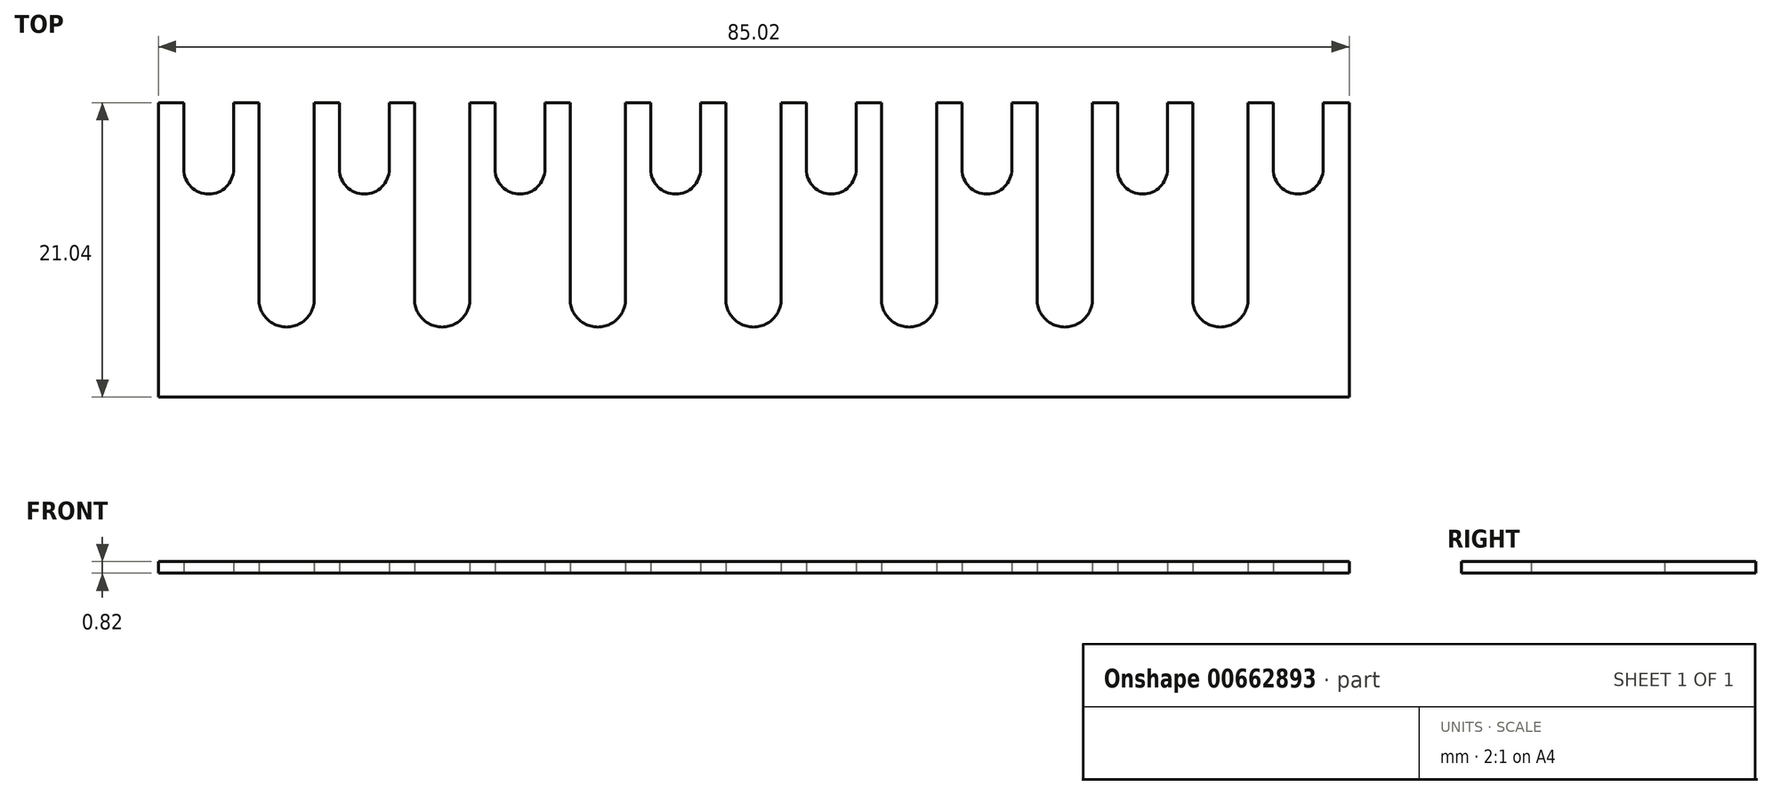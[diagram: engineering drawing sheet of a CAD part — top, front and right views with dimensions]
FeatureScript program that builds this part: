
annotation { "Feature Type Name" : "Feature", "Feature Type Description" : "" }
export const myFeature = defineFeature(function(context is Context, id is Id, definition is map)
    precondition{}
    {
        {
            var Q0;
            Q0=qCreatedBy(makeId("Top.planeOp"),FACE);
            var sketch = newSketch(context, id + "F0", { "sketchPlane" : qUnion([Q0])});
            skLineSegment(sketch, "E0.top", {"start": v(42.5, -10.52) * mm, "end": v(0, -10.52) * mm});
            skLineSegment(sketch, "E0.right", {"start": v(-42.5, 10.52) * mm, "end": v(-42.5, -10.52) * mm});
            skPoint(sketch, "E0.middle", {"position": v(0, 0) * mm});
            skPoint(sketch, "E1.endSnap0", {"position": v(0, 10.52) * mm});
            skLineSegment(sketch, "E2", {"start": v(-40.7, 5.77) * mm, "end": v(-40.7, 10.52) * mm});
            skLineSegment(sketch, "E3", {"start": v(-37.15, 10.52) * mm, "end": v(-37.15, 5.77) * mm});
            skLineSegment(sketch, "E4.trimOffspring", {"start": v(-40.7, 10.52) * mm, "end": v(-42.5, 10.52) * mm});
            skArc(sketch, "E5", {"start": v(-40.7, 5.77) * mm, "mid": v(-38.93, 3.99) * mm, "end": v(-37.15, 5.77) * mm});
            skLineSegment(sketch, "E6", {"start": v(-37.15, 10.52) * mm, "end": v(-35.34, 10.52) * mm});
            skLineSegment(sketch, "E7", {"start": v(-35.34, 10.52) * mm, "end": v(-35.34, -3.54) * mm});
            skLineSegment(sketch, "E8", {"start": v(0, -10.52) * mm, "end": v(-42.5, -10.52) * mm});
            skArc(sketch, "E9", {"start": v(-35.34, -3.54) * mm, "mid": v(-33.37, -5.51) * mm, "end": v(-31.4, -3.54) * mm});
            skLineSegment(sketch, "E10", {"start": v(-31.4, 10.52) * mm, "end": v(-31.4, -3.54) * mm});
            skLineSegment(sketch, "E11", {"start": v(-29.6, 5.77) * mm, "end": v(-29.6, 10.52) * mm});
            skLineSegment(sketch, "E12", {"start": v(-26.03, 10.52) * mm, "end": v(-26.03, 5.77) * mm});
            skLineSegment(sketch, "E13.trimOffspring", {"start": v(-29.6, 10.52) * mm, "end": v(-31.4, 10.52) * mm});
            skArc(sketch, "E14", {"start": v(-29.6, 5.77) * mm, "mid": v(-27.81, 3.99) * mm, "end": v(-26.03, 5.77) * mm});
            skLineSegment(sketch, "E15", {"start": v(-26.03, 10.52) * mm, "end": v(-24.23, 10.52) * mm});
            skLineSegment(sketch, "E16", {"start": v(-24.23, 10.52) * mm, "end": v(-24.23, -3.54) * mm});
            skArc(sketch, "E17", {"start": v(-24.23, -3.54) * mm, "mid": v(-22.26, -5.51) * mm, "end": v(-20.28, -3.54) * mm});
            skLineSegment(sketch, "E18", {"start": v(-20.28, 10.52) * mm, "end": v(-20.28, -3.54) * mm});
            skLineSegment(sketch, "E19", {"start": v(-18.48, 5.77) * mm, "end": v(-18.48, 10.52) * mm});
            skLineSegment(sketch, "E20", {"start": v(-14.92, 10.52) * mm, "end": v(-14.92, 5.77) * mm});
            skLineSegment(sketch, "E21.trimOffspring", {"start": v(-18.48, 10.52) * mm, "end": v(-20.28, 10.52) * mm});
            skArc(sketch, "E22", {"start": v(-18.48, 5.77) * mm, "mid": v(-16.7, 3.99) * mm, "end": v(-14.92, 5.77) * mm});
            skLineSegment(sketch, "E23", {"start": v(-14.92, 10.52) * mm, "end": v(-13.12, 10.52) * mm});
            skLineSegment(sketch, "E24", {"start": v(-13.12, 10.52) * mm, "end": v(-13.12, -3.54) * mm});
            skArc(sketch, "E25", {"start": v(-13.12, -3.54) * mm, "mid": v(-11.14, -5.51) * mm, "end": v(-9.17, -3.54) * mm});
            skLineSegment(sketch, "E26", {"start": v(-9.17, 10.52) * mm, "end": v(-9.17, -3.54) * mm});
            skLineSegment(sketch, "E27", {"start": v(-7.37, 5.77) * mm, "end": v(-7.37, 10.52) * mm});
            skLineSegment(sketch, "E28", {"start": v(-3.8, 10.52) * mm, "end": v(-3.8, 5.77) * mm});
            skLineSegment(sketch, "E29.trimOffspring", {"start": v(-7.37, 10.52) * mm, "end": v(-9.17, 10.52) * mm});
            skArc(sketch, "E30", {"start": v(-7.37, 5.77) * mm, "mid": v(-5.59, 3.99) * mm, "end": v(-3.8, 5.77) * mm});
            skLineSegment(sketch, "E31", {"start": v(-3.8, 10.52) * mm, "end": v(-2, 10.52) * mm});
            skLineSegment(sketch, "E32", {"start": v(-2, 10.52) * mm, "end": v(-2, -3.54) * mm});
            skArc(sketch, "E33", {"start": v(-2, -3.54) * mm, "mid": v(-0.03, -5.51) * mm, "end": v(1.94, -3.54) * mm});
            skLineSegment(sketch, "E34", {"start": v(1.94, 10.52) * mm, "end": v(1.94, -3.54) * mm});
            skLineSegment(sketch, "E35", {"start": v(3.75, 5.77) * mm, "end": v(3.75, 10.52) * mm});
            skLineSegment(sketch, "E36", {"start": v(7.3, 10.52) * mm, "end": v(7.3, 5.77) * mm});
            skLineSegment(sketch, "E37.trimOffspring", {"start": v(3.75, 10.52) * mm, "end": v(1.94, 10.52) * mm});
            skArc(sketch, "E38", {"start": v(3.75, 5.77) * mm, "mid": v(5.52, 3.99) * mm, "end": v(7.3, 5.77) * mm});
            skLineSegment(sketch, "E39", {"start": v(7.3, 10.52) * mm, "end": v(9.1, 10.52) * mm});
            skLineSegment(sketch, "E40", {"start": v(9.1, 10.52) * mm, "end": v(9.1, -3.54) * mm});
            skArc(sketch, "E41", {"start": v(9.1, -3.54) * mm, "mid": v(11.08, -5.51) * mm, "end": v(13.06, -3.54) * mm});
            skLineSegment(sketch, "E42", {"start": v(13.06, 10.52) * mm, "end": v(13.06, -3.54) * mm});
            skLineSegment(sketch, "E43", {"start": v(14.86, 5.77) * mm, "end": v(14.86, 10.52) * mm});
            skLineSegment(sketch, "E44", {"start": v(18.42, 10.52) * mm, "end": v(18.42, 5.77) * mm});
            skLineSegment(sketch, "E45.trimOffspring", {"start": v(14.86, 10.52) * mm, "end": v(13.06, 10.52) * mm});
            skArc(sketch, "E46", {"start": v(14.86, 5.77) * mm, "mid": v(16.64, 3.99) * mm, "end": v(18.42, 5.77) * mm});
            skLineSegment(sketch, "E47", {"start": v(18.42, 10.52) * mm, "end": v(20.22, 10.52) * mm});
            skLineSegment(sketch, "E48", {"start": v(20.22, 10.52) * mm, "end": v(20.22, -3.54) * mm});
            skArc(sketch, "E49", {"start": v(20.22, -3.54) * mm, "mid": v(22.2, -5.51) * mm, "end": v(24.17, -3.54) * mm});
            skLineSegment(sketch, "E50", {"start": v(24.17, 10.52) * mm, "end": v(24.17, -3.54) * mm});
            skLineSegment(sketch, "E51", {"start": v(25.97, 5.77) * mm, "end": v(25.97, 10.52) * mm});
            skLineSegment(sketch, "E52", {"start": v(29.53, 10.52) * mm, "end": v(29.53, 5.77) * mm});
            skLineSegment(sketch, "E53.trimOffspring", {"start": v(25.97, 10.52) * mm, "end": v(24.17, 10.52) * mm});
            skArc(sketch, "E54", {"start": v(25.97, 5.77) * mm, "mid": v(27.75, 3.99) * mm, "end": v(29.53, 5.77) * mm});
            skLineSegment(sketch, "E55", {"start": v(29.53, 10.52) * mm, "end": v(31.33, 10.52) * mm});
            skLineSegment(sketch, "E56", {"start": v(31.33, 10.52) * mm, "end": v(31.33, -3.54) * mm});
            skArc(sketch, "E57", {"start": v(31.33, -3.54) * mm, "mid": v(33.3, -5.51) * mm, "end": v(35.28, -3.54) * mm});
            skLineSegment(sketch, "E58", {"start": v(35.28, 10.52) * mm, "end": v(35.28, -3.54) * mm});
            skLineSegment(sketch, "E59", {"start": v(37.08, 5.77) * mm, "end": v(37.08, 10.52) * mm});
            skLineSegment(sketch, "E60", {"start": v(40.64, 10.52) * mm, "end": v(40.64, 5.77) * mm});
            skLineSegment(sketch, "E61.trimOffspring", {"start": v(37.08, 10.52) * mm, "end": v(35.28, 10.52) * mm});
            skArc(sketch, "E62", {"start": v(37.08, 5.77) * mm, "mid": v(38.86, 3.99) * mm, "end": v(40.64, 5.77) * mm});
            skLineSegment(sketch, "E63", {"start": v(40.64, 10.52) * mm, "end": v(42.5, 10.52) * mm});
            skLineSegment(sketch, "E64", {"start": v(42.5, -10.52) * mm, "end": v(42.5, 10.52) * mm});
            skSolve(sketch);
        }
        {
            var Q0;
            Q0 = qSketchRegion(id + "F0", true);
            extrude(context, id + "F1", {"entities" : qUnion([Q0]), "endBound" : BoundingType.SYMMETRIC, "depth" : 0.81 * mm, "offsetDistance" : 25.4 * mm});
        }
    });
